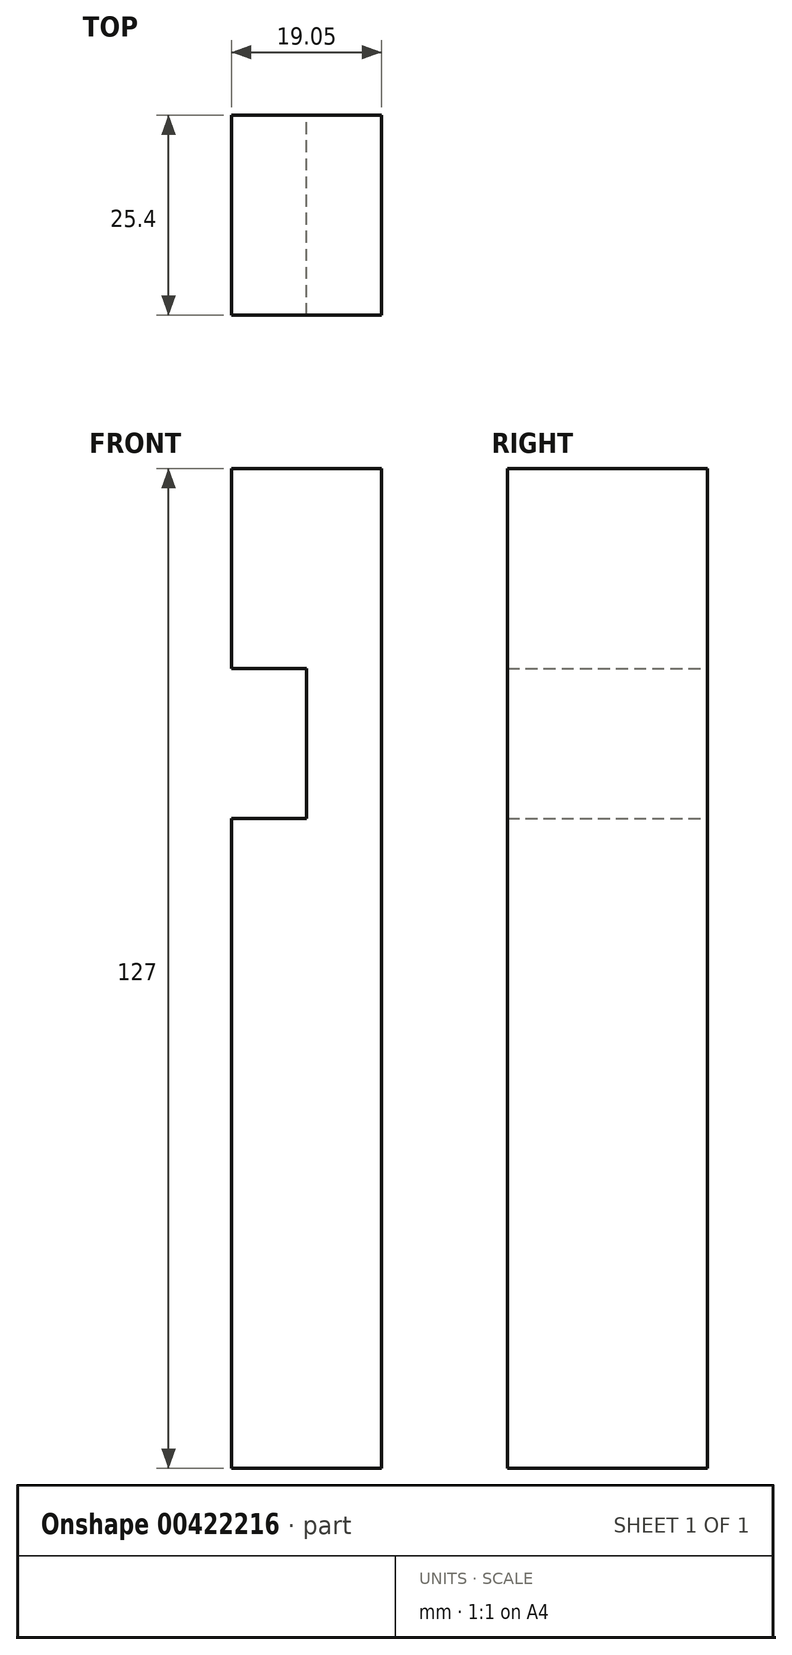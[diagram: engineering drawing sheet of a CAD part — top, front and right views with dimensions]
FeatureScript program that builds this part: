
annotation { "Feature Type Name" : "Feature", "Feature Type Description" : "" }
export const myFeature = defineFeature(function(context is Context, id is Id, definition is map)
    precondition{}
    {
        {
            var Q0;
            Q0=qCreatedBy(makeId("Front.planeOp"),FACE);
            var sketch = newSketch(context, id + "F0", { "sketchPlane" : qUnion([Q0])});
            skLineSegment(sketch, "E0", {"start": v(-58.62, -71.04) * mm, "end": v(-39.57, -71.04) * mm});
            skLineSegment(sketch, "E1", {"start": v(-39.57, -71.04) * mm, "end": v(-39.57, 55.96) * mm});
            skLineSegment(sketch, "E2", {"start": v(-39.57, 55.96) * mm, "end": v(-58.62, 55.96) * mm});
            skLineSegment(sketch, "E3", {"start": v(-58.62, 55.96) * mm, "end": v(-58.62, 30.56) * mm});
            skLineSegment(sketch, "E4", {"start": v(-58.62, 30.56) * mm, "end": v(-49.1, 30.56) * mm});
            skLineSegment(sketch, "E5", {"start": v(-49.1, 30.56) * mm, "end": v(-49.1, 11.51) * mm});
            skLineSegment(sketch, "E6", {"start": v(-49.1, 11.51) * mm, "end": v(-58.62, 11.51) * mm});
            skLineSegment(sketch, "E7", {"start": v(-58.62, 11.51) * mm, "end": v(-58.62, -71.04) * mm});
            skSolve(sketch);
        }
        {
            var Q0;
            Q0=makeQuery(id+"F0.imprint","IMPRINT",FACE,{"disambiguationData":[TD([[makeQuery(id+"F0.imprint","IMPRINT",EDGE,{"derivedFrom":sQuery(id+"F0.wireOp",EDGE,"E0")}),1.0]])]});
            extrude(context, id + "F1", {"entities" : qUnion([Q0]), "depth" : 25.4 * mm});
        }
    });
